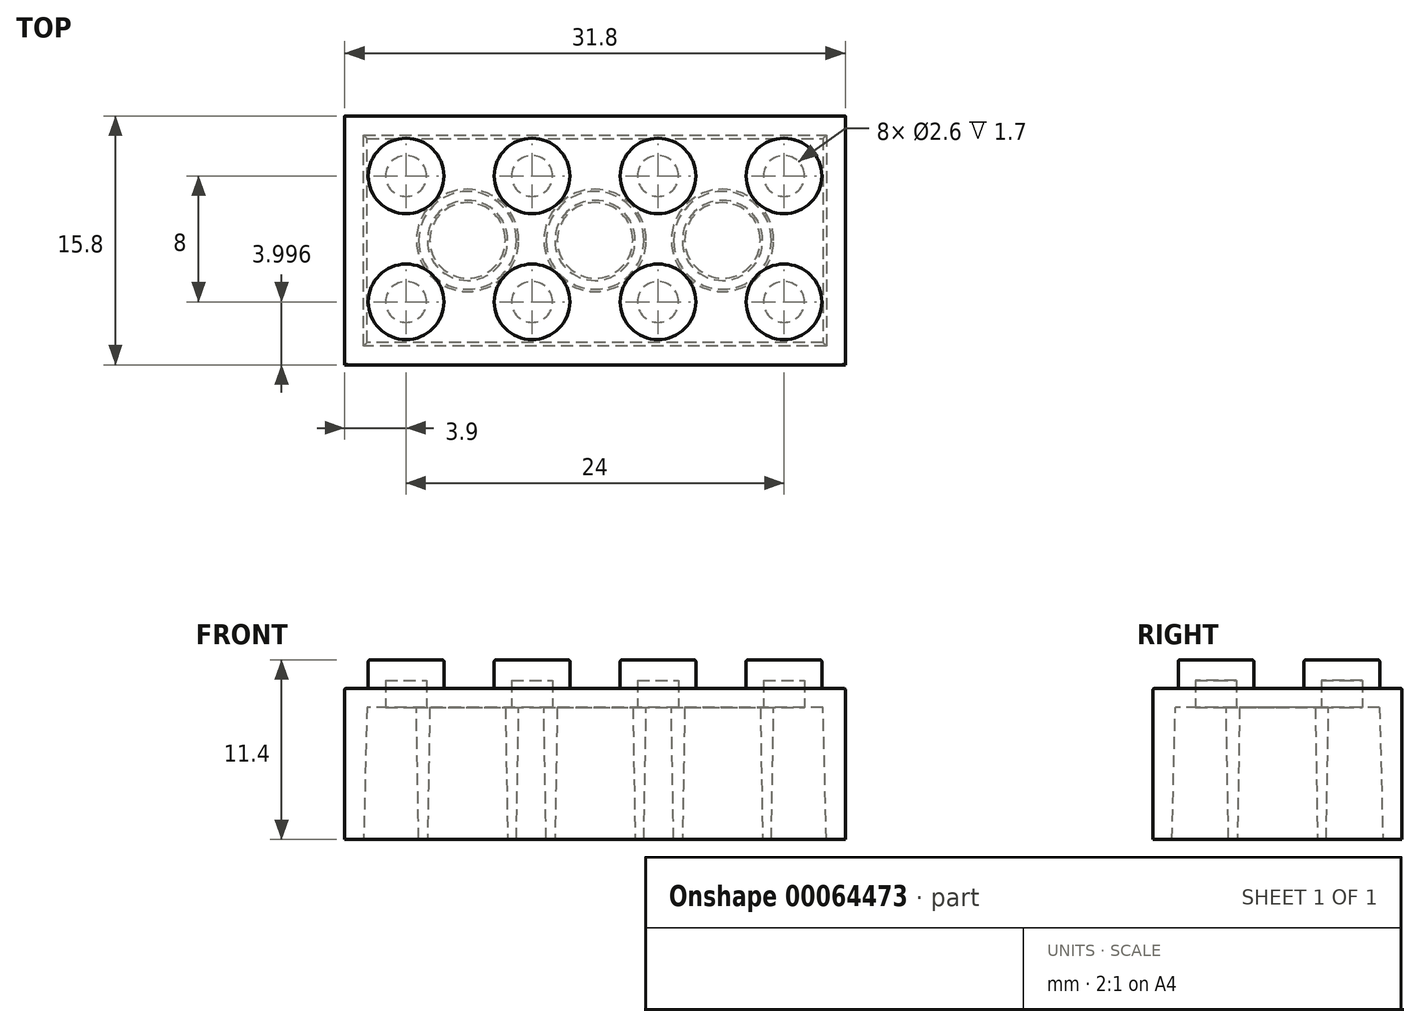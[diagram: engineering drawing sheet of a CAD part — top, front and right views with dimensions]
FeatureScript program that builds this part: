
annotation { "Feature Type Name" : "Feature", "Feature Type Description" : "" }
export const myFeature = defineFeature(function(context is Context, id is Id, definition is map)
    precondition{}
    {
        {
            var Q0;
            Q0=qCreatedBy(makeId("Top.planeOp"),FACE);
            var sketch = newSketch(context, id + "F0", { "sketchPlane" : qUnion([Q0])});
            skLineSegment(sketch, "E0.rect.bottom", {"start": v(15.9, -7.9) * mm, "end": v(-15.9, -7.9) * mm});
            skLineSegment(sketch, "E0.rect.top", {"start": v(15.9, 7.9) * mm, "end": v(-15.9, 7.9) * mm});
            skLineSegment(sketch, "E0.rect.left", {"start": v(15.9, -7.9) * mm, "end": v(15.9, 7.9) * mm});
            skLineSegment(sketch, "E0.rect.right", {"start": v(-15.9, -7.9) * mm, "end": v(-15.9, 7.9) * mm});
            skPoint(sketch, "E0.rect.middle", {"position": v(0, 0) * mm});
            skSolve(sketch);
        }
        {
            var Q0;
            Q0=makeQuery(id+"F0.imprint","IMPRINT",FACE,{"disambiguationData":[TD([[makeQuery(id+"F0.imprint","IMPRINT",EDGE,{"derivedFrom":sQuery(id+"F0.wireOp",EDGE,"E0.rect.bottom")}),-1.0]])]});
            extrude(context, id + "F1", {"entities" : qUnion([Q0]), "depth" : 9.6 * mm});
        }
        {
            var Q0;
            Q0=makeQuery(id+"F1.opExtrude","CAP_FACE",FACE,{"disambiguationData":[OSD([sQuery(id+"F0.wireOp",EDGE,"E0.rect.bottom"),sQuery(id+"F0.wireOp",EDGE,"E0.rect.top"),sQuery(id+"F0.wireOp",EDGE,"E0.rect.left"),sQuery(id+"F0.wireOp",EDGE,"E0.rect.right")])],"isStart":false});
            var sketch = newSketch(context, id + "F2", { "sketchPlane" : qUnion([Q0])});
            skCircle(sketch, "E1", {"center": v(12, -3.9) * mm, "radius": 2.4 * mm});
            skCircle(sketch, "E2.0.1.0", {"center": v(12, 4.1) * mm, "radius": 2.4 * mm});
            skCircle(sketch, "E2.1.0.0", {"center": v(4, -3.9) * mm, "radius": 2.4 * mm});
            skCircle(sketch, "E2.1.1.0", {"center": v(4, 4.1) * mm, "radius": 2.4 * mm});
            skCircle(sketch, "E2.2.0.0", {"center": v(-4, -3.9) * mm, "radius": 2.4 * mm});
            skCircle(sketch, "E2.2.1.0", {"center": v(-4, 4.1) * mm, "radius": 2.4 * mm});
            skCircle(sketch, "E2.3.0.0", {"center": v(-12, -3.9) * mm, "radius": 2.4 * mm});
            skCircle(sketch, "E2.3.1.0", {"center": v(-12, 4.1) * mm, "radius": 2.4 * mm});
            skLineSegment(sketch, "E2.direction1", {"start": v(12, -3.9) * mm, "end": v(4, -3.9) * mm, "construction": true});
            skLineSegment(sketch, "E2.direction2", {"start": v(12, -3.9) * mm, "end": v(12, 4.1) * mm, "construction": true});
            skSolve(sketch);
        }
        {
            var Q0;
            Q0 = qSketchRegion(id + "F2", true);
            extrude(context, id + "F3", {"entities" : qUnion([Q0]), "operationType" : NewBodyOperationType.ADD, "depth" : 1.8 * mm});
        }
        {
            var Q0;
            Q0=makeQuery(id+"F1.opExtrude","CAP_FACE",FACE,{"disambiguationData":[OSD([sQuery(id+"F0.wireOp",EDGE,"E0.rect.bottom"),sQuery(id+"F0.wireOp",EDGE,"E0.rect.top"),sQuery(id+"F0.wireOp",EDGE,"E0.rect.left"),sQuery(id+"F0.wireOp",EDGE,"E0.rect.right")])],"isStart":true});
            var sketch = newSketch(context, id + "F4", { "sketchPlane" : qUnion([Q0])});
            skLineSegment(sketch, "E3.0", {"start": v(14.7, 6.7) * mm, "end": v(-14.7, 6.7) * mm});
            skLineSegment(sketch, "E3.1", {"start": v(14.7, 6.7) * mm, "end": v(14.7, -6.7) * mm});
            skLineSegment(sketch, "E3.2", {"start": v(14.7, -6.7) * mm, "end": v(-14.7, -6.7) * mm});
            skLineSegment(sketch, "E3.3", {"start": v(-14.7, 6.7) * mm, "end": v(-14.7, -6.7) * mm});
            skSolve(sketch);
        }
        {
            var Q0;
            Q0 = qSketchRegion(id + "F4", true);
            extrude(context, id + "F5", {"entities" : qUnion([Q0]), "operationType" : NewBodyOperationType.REMOVE, "oppositeDirection" : true, "depth" : (9.6 - 1.2) * mm, "hasDraft" : true, "draftAngle" : 1.5 * degree, "draftPullDirection" : true});
        }
        {
            var Q0;
            Q0=makeQuery(id+"F5.boolean.opBoolean","COPY",FACE,{"derivedFrom":makeQuery(id+"F5.opExtrude","CAP_FACE",FACE,{"disambiguationData":[OSD([sQuery(id+"F4.wireOp",EDGE,"E3.0"),sQuery(id+"F4.wireOp",EDGE,"E3.1"),sQuery(id+"F4.wireOp",EDGE,"E3.2"),sQuery(id+"F4.wireOp",EDGE,"E3.3")])],"isStart":false})});
            var sketch = newSketch(context, id + "F6", { "sketchPlane" : qUnion([Q0])});
            skCircle(sketch, "E4.0", {"center": v(12, 3.9) * mm, "radius": 2.4 * mm, "construction": true});
            skCircle(sketch, "E5.0", {"center": v(4, 3.9) * mm, "radius": 2.4 * mm, "construction": true});
            skCircle(sketch, "E6.0", {"center": v(-4, 3.9) * mm, "radius": 2.4 * mm, "construction": true});
            skCircle(sketch, "E7.0", {"center": v(-12, 3.9) * mm, "radius": 2.4 * mm, "construction": true});
            skCircle(sketch, "E8.0", {"center": v(-12, -4.1) * mm, "radius": 2.4 * mm, "construction": true});
            skCircle(sketch, "E9.0", {"center": v(-4, -4.1) * mm, "radius": 2.4 * mm, "construction": true});
            skCircle(sketch, "E10.0", {"center": v(4, -4.1) * mm, "radius": 2.4 * mm, "construction": true});
            skCircle(sketch, "E11.0", {"center": v(12, -4.1) * mm, "radius": 2.4 * mm, "construction": true});
            skCircle(sketch, "E12", {"center": v(-12, 3.9) * mm, "radius": 1.3 * mm});
            skCircle(sketch, "E13", {"center": v(-4, 3.9) * mm, "radius": 1.3 * mm});
            skCircle(sketch, "E14", {"center": v(4, 3.9) * mm, "radius": 1.3 * mm});
            skCircle(sketch, "E15", {"center": v(12, 3.9) * mm, "radius": 1.3 * mm});
            skCircle(sketch, "E16", {"center": v(12, -4.1) * mm, "radius": 1.3 * mm});
            skCircle(sketch, "E17", {"center": v(4, -4.1) * mm, "radius": 1.3 * mm});
            skCircle(sketch, "E18", {"center": v(-4, -4.1) * mm, "radius": 1.3 * mm});
            skCircle(sketch, "E19", {"center": v(-12, -4.1) * mm, "radius": 1.3 * mm});
            skSolve(sketch);
        }
        {
            var Q0;
            Q0 = qSketchRegion(id + "F6", true);
            extrude(context, id + "F7", {"entities" : qUnion([Q0]), "operationType" : NewBodyOperationType.REMOVE, "oppositeDirection" : true, "depth" : 1.7 * mm});
        }
        {
            var Q0;
            Q0=makeQuery(id+"F5.boolean.opBoolean","COPY",FACE,{"derivedFrom":makeQuery(id+"F5.opExtrude","CAP_FACE",FACE,{"disambiguationData":[OSD([sQuery(id+"F4.wireOp",EDGE,"E3.0"),sQuery(id+"F4.wireOp",EDGE,"E3.1"),sQuery(id+"F4.wireOp",EDGE,"E3.2"),sQuery(id+"F4.wireOp",EDGE,"E3.3")])],"isStart":false})});
            var sketch = newSketch(context, id + "F8", { "sketchPlane" : qUnion([Q0])});
            skLineSegment(sketch, "E20.0", {"start": v(-15.9, 7.9) * mm, "end": v(-15.9, -7.9) * mm, "construction": true});
            skLineSegment(sketch, "E21", {"start": v(-15.9, 0) * mm, "end": v(17.94, 0) * mm});
            skPoint(sketch, "E21.endSnap0", {"position": v(-15.9, 0) * mm});
            skCircle(sketch, "E22", {"center": v(0, 0) * mm, "radius": 3.25 * mm});
            skCircle(sketch, "E23", {"center": v(8.1, 0) * mm, "radius": 3.25 * mm});
            skCircle(sketch, "E24", {"center": v(-8.1, 0) * mm, "radius": 3.25 * mm});
            skCircle(sketch, "E25", {"center": v(-8.1, 0) * mm, "radius": 2.4 * mm});
            skCircle(sketch, "E26", {"center": v(0, 0) * mm, "radius": 2.4 * mm});
            skCircle(sketch, "E27", {"center": v(8.1, 0) * mm, "radius": 2.4 * mm});
            skLineSegment(sketch, "E28", {"start": v(-12, 3.9) * mm, "end": v(-4, -4.1) * mm, "construction": true});
            skSolve(sketch);
        }
        {
            var Q0;
            Q0 = qSketchRegion(id + "F8", true);
            var Q1;
            Q1=makeQuery(id+"F1.opExtrude","CAP_FACE",FACE,{"disambiguationData":[OSD([sQuery(id+"F0.wireOp",EDGE,"E0.rect.bottom"),sQuery(id+"F0.wireOp",EDGE,"E0.rect.top"),sQuery(id+"F0.wireOp",EDGE,"E0.rect.left"),sQuery(id+"F0.wireOp",EDGE,"E0.rect.right")])],"isStart":true});
            extrude(context, id + "F9", {"entities" : qUnion([Q0]), "operationType" : NewBodyOperationType.ADD, "endBound" : BoundingType.UP_TO_SURFACE, "endBoundEntityFace" : qUnion([Q1]), "depth" : 25 * mm, "hasDraft" : true, "draftAngle" : 1 * degree, "draftPullDirection" : true});
        }
        {
            var Q0;
            Q0=makeQuery(id+"F3.opExtrude","CAP_EDGE",EDGE,{"disambiguationData":[OSD([sQuery(id+"F2.wireOp",EDGE,"E2.1.0.0")])],"isStart":false});
            var Q1;
            Q1=makeQuery(id+"F3.opExtrude","CAP_EDGE",EDGE,{"disambiguationData":[OSD([sQuery(id+"F2.wireOp",EDGE,"E2.3.0.0")])],"isStart":false});
            var Q2;
            Q2=makeQuery(id+"F3.opExtrude","CAP_EDGE",EDGE,{"disambiguationData":[OSD([sQuery(id+"F2.wireOp",EDGE,"E2.3.1.0")])],"isStart":false});
            var Q3;
            Q3=makeQuery(id+"F3.opExtrude","CAP_EDGE",EDGE,{"disambiguationData":[OSD([sQuery(id+"F2.wireOp",EDGE,"E2.2.1.0")])],"isStart":false});
            var Q4;
            Q4=makeQuery(id+"F3.opExtrude","CAP_EDGE",EDGE,{"disambiguationData":[OSD([sQuery(id+"F2.wireOp",EDGE,"E2.2.0.0")])],"isStart":false});
            var Q5;
            Q5=makeQuery(id+"F3.opExtrude","CAP_EDGE",EDGE,{"disambiguationData":[OSD([sQuery(id+"F2.wireOp",EDGE,"E2.1.1.0")])],"isStart":false});
            var Q6;
            Q6=makeQuery(id+"F3.opExtrude","CAP_EDGE",EDGE,{"disambiguationData":[OSD([sQuery(id+"F2.wireOp",EDGE,"E2.0.1.0")])],"isStart":false});
            var Q7;
            Q7=makeQuery(id+"F3.opExtrude","CAP_EDGE",EDGE,{"disambiguationData":[OSD([sQuery(id+"F2.wireOp",EDGE,"E1")])],"isStart":false});
            var Q8;
            Q8=makeQuery(id+"F1.opExtrude","CAP_EDGE",EDGE,{"disambiguationData":[OSD([sQuery(id+"F0.wireOp",EDGE,"E0.rect.left")])],"isStart":false});
            var Q9;
            Q9=makeQuery(id+"F1.opExtrude","CAP_EDGE",EDGE,{"disambiguationData":[OSD([sQuery(id+"F0.wireOp",EDGE,"E0.rect.top")])],"isStart":false});
            var Q10;
            Q10=makeQuery(id+"F1.opExtrude","CAP_EDGE",EDGE,{"disambiguationData":[OSD([sQuery(id+"F0.wireOp",EDGE,"E0.rect.right")])],"isStart":false});
            var Q11;
            Q11=makeQuery(id+"F1.opExtrude","CAP_EDGE",EDGE,{"disambiguationData":[OSD([sQuery(id+"F0.wireOp",EDGE,"E0.rect.bottom")])],"isStart":false});
            fillet(context, id + "F10", {"entities" : qUnion([Q0, Q1, Q2, Q3, Q4, Q5, Q6, Q7, Q8, Q9, Q10, Q11]), "radius" : .1 * mm, "tangentPropagation" : true, "allowEdgeOverflow" : false});
        }
    });
